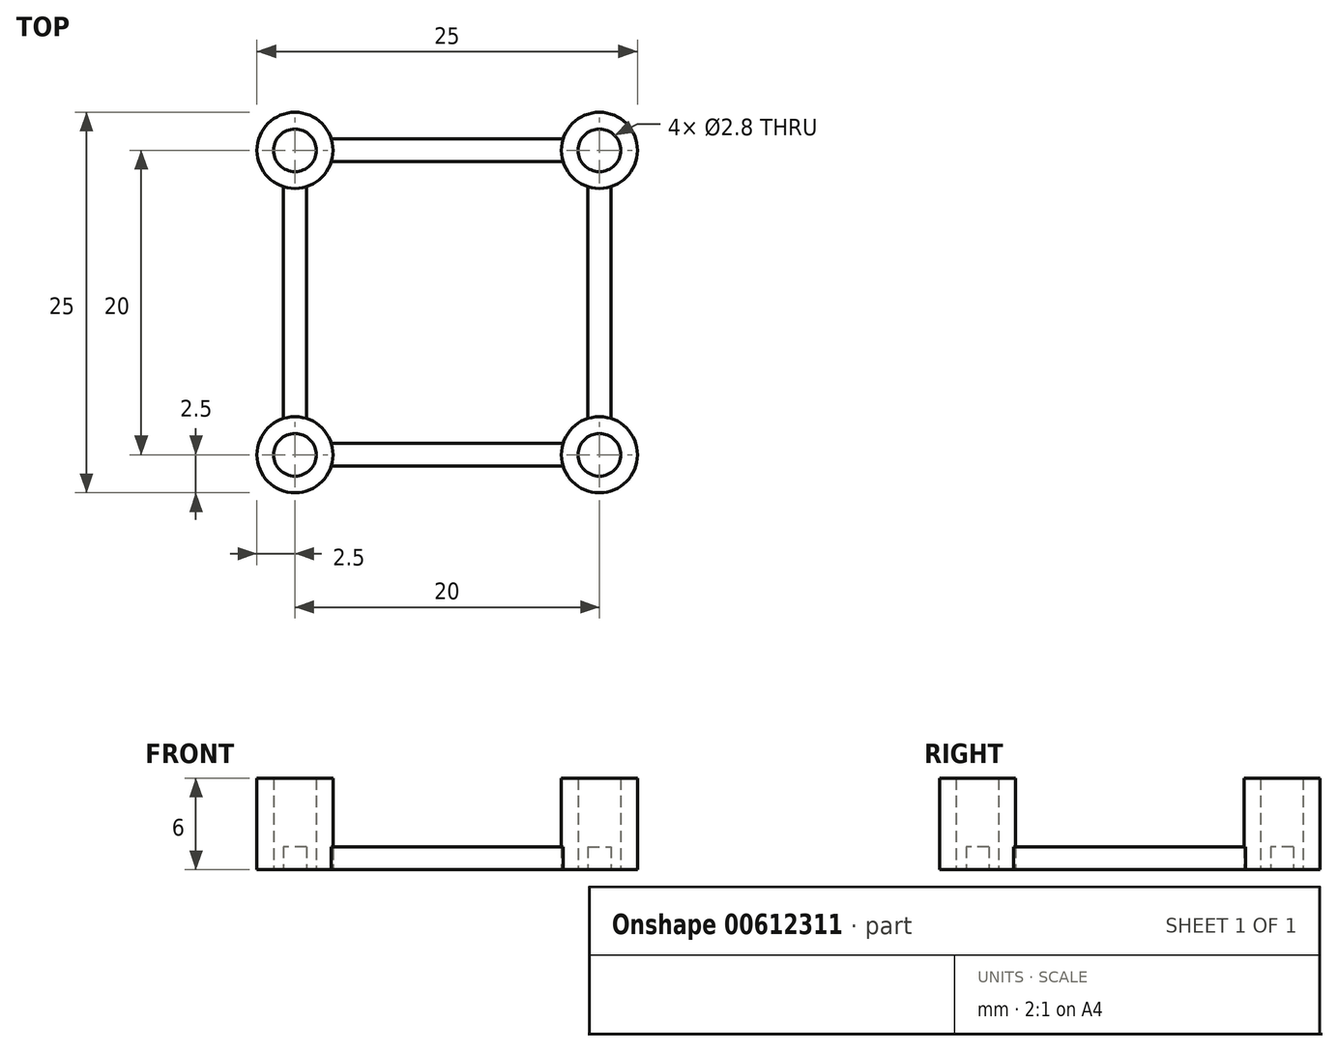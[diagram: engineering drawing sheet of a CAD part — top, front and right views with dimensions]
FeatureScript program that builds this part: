
annotation { "Feature Type Name" : "Feature", "Feature Type Description" : "" }
export const myFeature = defineFeature(function(context is Context, id is Id, definition is map)
    precondition{}
    {
        {
            var Q0;
            Q0=qCreatedBy(makeId("Top.planeOp"),FACE);
            var sketch = newSketch(context, id + "F0", { "sketchPlane" : qUnion([Q0])});
            skCircle(sketch, "E0", {"center": v(-10, 10) * mm, "radius": 1.4 * mm});
            skCircle(sketch, "E1", {"center": v(10, 10) * mm, "radius": 1.4 * mm});
            skCircle(sketch, "E2", {"center": v(10, -10) * mm, "radius": 2.5 * mm});
            skCircle(sketch, "E3", {"center": v(-10, -10) * mm, "radius": 1.4 * mm});
            skCircle(sketch, "E4", {"center": v(-10, -10) * mm, "radius": 2.5 * mm});
            skCircle(sketch, "E5", {"center": v(-10, 10) * mm, "radius": 2.5 * mm});
            skCircle(sketch, "E6", {"center": v(10, 10) * mm, "radius": 2.5 * mm});
            skCircle(sketch, "E7", {"center": v(10, -10) * mm, "radius": 1.4 * mm});
            skLineSegment(sketch, "E8.bottom", {"start": v(10.75, 10.75) * mm, "end": v(-10.75, 10.75) * mm});
            skLineSegment(sketch, "E8.top", {"start": v(10.75, -10.75) * mm, "end": v(-10.75, -10.75) * mm});
            skLineSegment(sketch, "E8.left", {"start": v(10.75, 10.75) * mm, "end": v(10.75, -10.75) * mm});
            skLineSegment(sketch, "E8.right", {"start": v(-10.75, 10.75) * mm, "end": v(-10.75, -10.75) * mm});
            skPoint(sketch, "E8.middle", {"position": v(0, 0) * mm});
            skLineSegment(sketch, "E9.bottom", {"start": v(9.25, -9.25) * mm, "end": v(-9.25, -9.25) * mm});
            skLineSegment(sketch, "E9.top", {"start": v(9.25, 9.25) * mm, "end": v(-9.25, 9.25) * mm});
            skLineSegment(sketch, "E9.left", {"start": v(9.25, -9.25) * mm, "end": v(9.25, 9.25) * mm});
            skLineSegment(sketch, "E9.right", {"start": v(-9.25, -9.25) * mm, "end": v(-9.25, 9.25) * mm});
            skSolve(sketch);
        }
        {
            var Q0;
            {var subQ0=sQuery(id+"F0.wireOp",EDGE,"E8.right");var subQ1=sQuery(id+"F0.wireOp",EDGE,"E0");var subQ2=makeQuery(id+"F0.imprint","INTERSECT",VERTEX,{"derivedFrom":[subQ1,subQ0]});Q0=makeQuery(id+"F0.imprint","IMPRINT",FACE,{"disambiguationData":[TD([[makeQuery(id+"F0.imprint","IMPRINT",EDGE,{"disambiguationData":[TD([[subQ2,1.0]])],"derivedFrom":subQ1}),-1.0]])]});}
            var Q1;
            {var subQ0=sQuery(id+"F0.wireOp",EDGE,"E8.right");var subQ1=sQuery(id+"F0.wireOp",EDGE,"E0");var subQ2=makeQuery(id+"F0.imprint","INTERSECT",VERTEX,{"derivedFrom":[subQ1,subQ0]});Q1=makeQuery(id+"F0.imprint","IMPRINT",FACE,{"disambiguationData":[TD([[makeQuery(id+"F0.imprint","IMPRINT",EDGE,{"disambiguationData":[TD([[subQ2,-1.0]])],"derivedFrom":subQ1}),-1.0]])]});}
            var Q2;
            {var subQ0=sQuery(id+"F0.wireOp",EDGE,"E8.bottom");var subQ1=sQuery(id+"F0.wireOp",EDGE,"E0");var subQ2=makeQuery(id+"F0.imprint","INTERSECT",VERTEX,{"derivedFrom":[subQ1,subQ0]});Q2=makeQuery(id+"F0.imprint","IMPRINT",FACE,{"disambiguationData":[TD([[makeQuery(id+"F0.imprint","IMPRINT",EDGE,{"disambiguationData":[TD([[subQ2,1.0]])],"derivedFrom":subQ1}),-1.0]])]});}
            var Q3;
            {var subQ0=sQuery(id+"F0.wireOp",EDGE,"E9.right");var subQ1=sQuery(id+"F0.wireOp",EDGE,"E0");var subQ2=makeQuery(id+"F0.imprint","INTERSECT",VERTEX,{"derivedFrom":[subQ1,subQ0]});Q3=makeQuery(id+"F0.imprint","IMPRINT",FACE,{"disambiguationData":[TD([[makeQuery(id+"F0.imprint","IMPRINT",EDGE,{"disambiguationData":[TD([[subQ2,-1.0]])],"derivedFrom":subQ1}),-1.0]])]});}
            var Q4;
            {var subQ0=sQuery(id+"F0.wireOp",EDGE,"E9.top");var subQ1=sQuery(id+"F0.wireOp",EDGE,"E1");var subQ2=makeQuery(id+"F0.imprint","INTERSECT",VERTEX,{"derivedFrom":[subQ1,subQ0]});Q4=makeQuery(id+"F0.imprint","IMPRINT",FACE,{"disambiguationData":[TD([[makeQuery(id+"F0.imprint","IMPRINT",EDGE,{"disambiguationData":[TD([[subQ2,-1.0]])],"derivedFrom":subQ1}),-1.0]])]});}
            var Q5;
            {var subQ0=sQuery(id+"F0.wireOp",EDGE,"E9.top");var subQ1=sQuery(id+"F0.wireOp",EDGE,"E1");var subQ2=makeQuery(id+"F0.imprint","INTERSECT",VERTEX,{"derivedFrom":[subQ1,subQ0]});Q5=makeQuery(id+"F0.imprint","IMPRINT",FACE,{"disambiguationData":[TD([[makeQuery(id+"F0.imprint","IMPRINT",EDGE,{"disambiguationData":[TD([[subQ2,1.0]])],"derivedFrom":subQ1}),-1.0]])]});}
            var Q6;
            {var subQ0=sQuery(id+"F0.wireOp",EDGE,"E8.bottom");var subQ1=sQuery(id+"F0.wireOp",EDGE,"E1");var subQ2=makeQuery(id+"F0.imprint","INTERSECT",VERTEX,{"derivedFrom":[subQ1,subQ0]});Q6=makeQuery(id+"F0.imprint","IMPRINT",FACE,{"disambiguationData":[TD([[makeQuery(id+"F0.imprint","IMPRINT",EDGE,{"disambiguationData":[TD([[subQ2,1.0]])],"derivedFrom":subQ1}),-1.0]])]});}
            var Q7;
            {var subQ0=sQuery(id+"F0.wireOp",EDGE,"E9.left");var subQ1=sQuery(id+"F0.wireOp",EDGE,"E1");var subQ2=makeQuery(id+"F0.imprint","INTERSECT",VERTEX,{"derivedFrom":[subQ1,subQ0]});Q7=makeQuery(id+"F0.imprint","IMPRINT",FACE,{"disambiguationData":[TD([[makeQuery(id+"F0.imprint","IMPRINT",EDGE,{"disambiguationData":[TD([[subQ2,-1.0]])],"derivedFrom":subQ1}),-1.0]])]});}
            var Q8;
            {var subQ0=sQuery(id+"F0.wireOp",EDGE,"E8.left");var subQ1=sQuery(id+"F0.wireOp",EDGE,"E2");var subQ2=makeQuery(id+"F0.imprint","INTERSECT",VERTEX,{"derivedFrom":[subQ1,subQ0]});Q8=makeQuery(id+"F0.imprint","IMPRINT",FACE,{"disambiguationData":[TD([[makeQuery(id+"F0.imprint","IMPRINT",EDGE,{"disambiguationData":[TD([[subQ2,1.0]])],"derivedFrom":subQ1}),1.0]])]});}
            var Q9;
            {var subQ0=sQuery(id+"F0.wireOp",EDGE,"E8.top");var subQ1=sQuery(id+"F0.wireOp",EDGE,"E2");var subQ2=makeQuery(id+"F0.imprint","INTERSECT",VERTEX,{"derivedFrom":[subQ1,subQ0]});Q9=makeQuery(id+"F0.imprint","IMPRINT",FACE,{"disambiguationData":[TD([[makeQuery(id+"F0.imprint","IMPRINT",EDGE,{"disambiguationData":[TD([[subQ2,1.0]])],"derivedFrom":subQ1}),1.0]])]});}
            var Q10;
            {var subQ0=sQuery(id+"F0.wireOp",EDGE,"E9.left");var subQ1=sQuery(id+"F0.wireOp",EDGE,"E2");var subQ2=makeQuery(id+"F0.imprint","INTERSECT",VERTEX,{"derivedFrom":[subQ1,subQ0]});Q10=makeQuery(id+"F0.imprint","IMPRINT",FACE,{"disambiguationData":[TD([[makeQuery(id+"F0.imprint","IMPRINT",EDGE,{"disambiguationData":[TD([[subQ2,-1.0]])],"derivedFrom":subQ1}),1.0]])]});}
            var Q11;
            {var subQ0=sQuery(id+"F0.wireOp",EDGE,"E8.left");var subQ1=sQuery(id+"F0.wireOp",EDGE,"E2");var subQ2=makeQuery(id+"F0.imprint","INTERSECT",VERTEX,{"derivedFrom":[subQ1,subQ0]});Q11=makeQuery(id+"F0.imprint","IMPRINT",FACE,{"disambiguationData":[TD([[makeQuery(id+"F0.imprint","IMPRINT",EDGE,{"disambiguationData":[TD([[subQ2,-1.0]])],"derivedFrom":subQ1}),1.0]])]});}
            var Q12;
            {var subQ0=sQuery(id+"F0.wireOp",EDGE,"E9.right");var subQ1=sQuery(id+"F0.wireOp",EDGE,"E3");var subQ2=makeQuery(id+"F0.imprint","INTERSECT",VERTEX,{"derivedFrom":[subQ1,subQ0]});Q12=makeQuery(id+"F0.imprint","IMPRINT",FACE,{"disambiguationData":[TD([[makeQuery(id+"F0.imprint","IMPRINT",EDGE,{"disambiguationData":[TD([[subQ2,1.0]])],"derivedFrom":subQ1}),-1.0]])]});}
            var Q13;
            {var subQ0=sQuery(id+"F0.wireOp",EDGE,"E9.bottom");var subQ1=sQuery(id+"F0.wireOp",EDGE,"E3");var subQ2=makeQuery(id+"F0.imprint","INTERSECT",VERTEX,{"derivedFrom":[subQ1,subQ0]});Q13=makeQuery(id+"F0.imprint","IMPRINT",FACE,{"disambiguationData":[TD([[makeQuery(id+"F0.imprint","IMPRINT",EDGE,{"disambiguationData":[TD([[subQ2,1.0]])],"derivedFrom":subQ1}),-1.0]])]});}
            var Q14;
            {var subQ0=sQuery(id+"F0.wireOp",EDGE,"E8.right");var subQ1=sQuery(id+"F0.wireOp",EDGE,"E3");var subQ2=makeQuery(id+"F0.imprint","INTERSECT",VERTEX,{"derivedFrom":[subQ1,subQ0]});Q14=makeQuery(id+"F0.imprint","IMPRINT",FACE,{"disambiguationData":[TD([[makeQuery(id+"F0.imprint","IMPRINT",EDGE,{"disambiguationData":[TD([[subQ2,-1.0]])],"derivedFrom":subQ1}),-1.0]])]});}
            var Q15;
            {var subQ0=sQuery(id+"F0.wireOp",EDGE,"E9.right");var subQ1=sQuery(id+"F0.wireOp",EDGE,"E3");var subQ2=makeQuery(id+"F0.imprint","INTERSECT",VERTEX,{"derivedFrom":[subQ1,subQ0]});Q15=makeQuery(id+"F0.imprint","IMPRINT",FACE,{"disambiguationData":[TD([[makeQuery(id+"F0.imprint","IMPRINT",EDGE,{"disambiguationData":[TD([[subQ2,-1.0]])],"derivedFrom":subQ1}),-1.0]])]});}
            var Q16;
            {var subQ3=sQuery(id+"F0.wireOp",EDGE,"E3");var subQ7=sQuery(id+"F0.wireOp",EDGE,"E8.right");var subQ11=makeQuery(id+"F0.imprint","INTERSECT",VERTEX,{"disambiguationData":[OD(1.0)],"derivedFrom":[subQ3,subQ7]});Q16=makeQuery(id+"F0.imprint","IMPRINT",FACE,{"disambiguationData":[TD([[makeQuery(id+"F0.imprint","IMPRINT",EDGE,{"disambiguationData":[TD([[subQ11,1.0]])],"derivedFrom":subQ3}),-1.0]])]});}
            var Q17;
            {var subQ0=sQuery(id+"F0.wireOp",EDGE,"E9.right");var subQ1=sQuery(id+"F0.wireOp",EDGE,"E4");var subQ2=makeQuery(id+"F0.imprint","INTERSECT",VERTEX,{"derivedFrom":[subQ1,subQ0]});Q17=makeQuery(id+"F0.imprint","IMPRINT",FACE,{"disambiguationData":[TD([[makeQuery(id+"F0.imprint","IMPRINT",EDGE,{"disambiguationData":[TD([[subQ2,1.0]])],"derivedFrom":subQ1}),1.0]])]});}
            var Q18;
            {var subQ0=sQuery(id+"F0.wireOp",EDGE,"E9.right");var subQ1=sQuery(id+"F0.wireOp",EDGE,"E5");var subQ2=makeQuery(id+"F0.imprint","INTERSECT",VERTEX,{"derivedFrom":[subQ1,subQ0]});Q18=makeQuery(id+"F0.imprint","IMPRINT",FACE,{"disambiguationData":[TD([[makeQuery(id+"F0.imprint","IMPRINT",EDGE,{"disambiguationData":[TD([[subQ2,-1.0]])],"derivedFrom":subQ1}),1.0]])]});}
            var Q19;
            {var subQ0=sQuery(id+"F0.wireOp",EDGE,"E8.bottom");var subQ3=sQuery(id+"F0.wireOp",EDGE,"E1");var subQ4=makeQuery(id+"F0.imprint","INTERSECT",VERTEX,{"disambiguationData":[OD(1.0)],"derivedFrom":[subQ3,subQ0]});Q19=makeQuery(id+"F0.imprint","IMPRINT",FACE,{"disambiguationData":[TD([[makeQuery(id+"F0.imprint","IMPRINT",EDGE,{"disambiguationData":[TD([[subQ4,-1.0]])],"derivedFrom":subQ3}),-1.0]])]});}
            var Q20;
            {var subQ0=sQuery(id+"F0.wireOp",EDGE,"E9.top");var subQ1=sQuery(id+"F0.wireOp",EDGE,"E6");var subQ2=makeQuery(id+"F0.imprint","INTERSECT",VERTEX,{"derivedFrom":[subQ1,subQ0]});Q20=makeQuery(id+"F0.imprint","IMPRINT",FACE,{"disambiguationData":[TD([[makeQuery(id+"F0.imprint","IMPRINT",EDGE,{"disambiguationData":[TD([[subQ2,-1.0]])],"derivedFrom":subQ1}),1.0]])]});}
            extrude(context, id + "F1", {"entities" : qUnion([Q0, Q1, Q2, Q3, Q4, Q5, Q6, Q7, Q8, Q9, Q10, Q11, Q12, Q13, Q14, Q15, Q16, Q17, Q18, Q19, Q20]), "depth" : 6 * mm, "offsetDistance" : 25 * mm});
        }
        {
            var Q0;
            {var subQ0=sQuery(id+"F0.wireOp",EDGE,"E8.right");var subQ1=sQuery(id+"F0.wireOp",EDGE,"E4");var subQ2=makeQuery(id+"F0.imprint","INTERSECT",VERTEX,{"derivedFrom":[subQ1,subQ0]});Q0=makeQuery(id+"F0.imprint","IMPRINT",FACE,{"disambiguationData":[TD([[makeQuery(id+"F0.imprint","IMPRINT",EDGE,{"disambiguationData":[TD([[subQ2,1.0]])],"derivedFrom":subQ1}),-1.0]])]});}
            var Q1;
            {var subQ0=sQuery(id+"F0.wireOp",EDGE,"E8.bottom");var subQ1=sQuery(id+"F0.wireOp",EDGE,"E5");var subQ2=makeQuery(id+"F0.imprint","INTERSECT",VERTEX,{"derivedFrom":[subQ1,subQ0]});Q1=makeQuery(id+"F0.imprint","IMPRINT",FACE,{"disambiguationData":[TD([[makeQuery(id+"F0.imprint","IMPRINT",EDGE,{"disambiguationData":[TD([[subQ2,1.0]])],"derivedFrom":subQ1}),-1.0]])]});}
            var Q2;
            {var subQ0=sQuery(id+"F0.wireOp",EDGE,"E8.left");var subQ1=sQuery(id+"F0.wireOp",EDGE,"E2");var subQ2=makeQuery(id+"F0.imprint","INTERSECT",VERTEX,{"derivedFrom":[subQ1,subQ0]});Q2=makeQuery(id+"F0.imprint","IMPRINT",FACE,{"disambiguationData":[TD([[makeQuery(id+"F0.imprint","IMPRINT",EDGE,{"disambiguationData":[TD([[subQ2,-1.0]])],"derivedFrom":subQ1}),-1.0]])]});}
            var Q3;
            {var subQ0=sQuery(id+"F0.wireOp",EDGE,"E8.top");var subQ1=sQuery(id+"F0.wireOp",EDGE,"E2");var subQ2=makeQuery(id+"F0.imprint","INTERSECT",VERTEX,{"derivedFrom":[subQ1,subQ0]});Q3=makeQuery(id+"F0.imprint","IMPRINT",FACE,{"disambiguationData":[TD([[makeQuery(id+"F0.imprint","IMPRINT",EDGE,{"disambiguationData":[TD([[subQ2,1.0]])],"derivedFrom":subQ1}),-1.0]])]});}
            extrude(context, id + "F2", {"entities" : qUnion([Q0, Q1, Q2, Q3]), "depth" : 1.5 * mm, "offsetDistance" : 25 * mm});
        }
    });
